# Revit family: W-Wide Flange-Column
name_source: partatom
category: Structural Columns
revit_build: Autodesk Revit Architecture 2012 (Build: 20110210_1515)
units: mm (PartAtom-declared; Revit-internal decimal feet)

## types (287) — shared parameters
Assembly Code = B10

## per-type parameters (varying)
| type | A | W | bf | d | k | kr | tf | tw |
| W44X335 | 98.5 in² | 335 | 1' - 3 7/8" | 3' - 8" | 0' - 2 5/8" | 0' - 0 7/8" | 0' - 1 3/4" | 0' - 1" |
| W44X290 | 85.4 in² | 290 | 1' - 3 13/16" | 3' - 7 5/8" | 0' - 2 7/16" | 0' - 0 7/8" | 0' - 1 9/16" | 0' - 0 7/8" |
| W44X262 | 76.9 in² | 262 | 1' - 3 13/16" | 3' - 7 5/16" | 0' - 2 1/4" | 0' - 0 13/16" | 0' - 1 7/16" | 0' - 0 13/16" |
| W44X230 | 67.7 in² | 230 | 1' - 3 13/16" | 3' - 6 7/8" | 0' - 2 1/16" | 0' - 0 13/16" | 0' - 1 1/4" | 0' - 0 11/16" |
| W40X593 | 174 in² | 593 | 1' - 4 11/16" | 3' - 7" | 0' - 4 1/2" | 0' - 1 1/4" | 0' - 3 1/4" | 0' - 1 13/16" |
| W40X503 | 148 in² | 503 | 1' - 4 3/8" | 3' - 6 1/8" | 0' - 4" | 0' - 1 1/4" | 0' - 2 3/4" | 0' - 1 9/16" |
| W40X431 | 127 in² | 431 | 1' - 4 3/16" | 3' - 5 5/16" | 0' - 3 5/8" | 0' - 1 1/4" | 0' - 2 3/8" | 0' - 1 5/16" |
| W40X397 | 117 in² | 397 | 1' - 4 1/8" | 3' - 5" | 0' - 3 1/2" | 0' - 1 5/16" | 0' - 2 3/16" | 0' - 1 1/4" |
| W40X372 | 109 in² | 372 | 1' - 4 1/8" | 3' - 4 5/8" | 0' - 3 5/16" | 0' - 1 1/4" | 0' - 2 1/16" | 0' - 1 3/16" |
| W40X362 | 107 in² | 362 | 1' - 4" | 3' - 4 5/8" | 0' - 3 1/4" | 0' - 1 1/4" | 0' - 2" | 0' - 1 1/8" |
| W40X324 | 95.3 in² | 324 | 1' - 3 7/8" | 3' - 4 3/16" | 0' - 3 1/16" | 0' - 1 1/4" | 0' - 1 13/16" | 0' - 1" |
| W40X297 | 87.4 in² | 297 | 1' - 3 13/16" | 3' - 3 13/16" | 0' - 2 15/16" | 0' - 1 5/16" | 0' - 1 5/8" | 0' - 0 15/16" |
| W40X277 | 81.4 in² | 277 | 1' - 3 13/16" | 3' - 3 11/16" | 0' - 2 7/8" | 0' - 1 5/16" | 0' - 1 9/16" | 0' - 0 13/16" |
| W40X249 | 73.3 in² | 249 | 1' - 3 13/16" | 3' - 3 3/8" | 0' - 2 11/16" | 0' - 1 1/4" | 0' - 1 7/16" | 0' - 0 3/4" |
| W40X215 | 63.4 in² | 215 | 1' - 3 13/16" | 3' - 3" | 0' - 2 1/2" | 0' - 1 1/4" | 0' - 1 1/4" | 0' - 0 5/8" |
| W40X199 | 58.5 in² | 199 | 1' - 3 13/16" | 3' - 2 11/16" | 0' - 2 5/16" | 0' - 1 1/4" | 0' - 1 1/16" | 0' - 0 5/8" |
| W40X392 | 115 in² | 392 | 1' - 0 3/8" | 3' - 5 5/8" | 0' - 3 13/16" | 0' - 1 5/16" | 0' - 2 1/2" | 0' - 1 7/16" |
| W40X331 | 97.5 in² | 331 | 1' - 0 3/16" | 3' - 4 13/16" | 0' - 3 3/8" | 0' - 1 1/4" | 0' - 2 1/8" | 0' - 1 1/4" |
| W40X327 | 96 in² | 327 | 1' - 0 1/8" | 3' - 4 13/16" | 0' - 3 3/8" | 0' - 1 1/4" | 0' - 2 1/8" | 0' - 1 3/16" |
| W40X294 | 86.3 in² | 294 | 1' - 0" | 3' - 4 3/8" | 0' - 3 3/16" | 0' - 1 1/4" | 0' - 1 15/16" | 0' - 1 1/16" |
| W40X278 | 82 in² | 278 | 1' - 0" | 3' - 4 3/16" | 0' - 3 1/16" | 0' - 1 1/4" | 0' - 1 13/16" | 0' - 1" |
| W40X264 | 77.6 in² | 264 | 0' - 11 7/8" | 3' - 4" | 0' - 3" | 0' - 1 1/4" | 0' - 1 3/4" | 0' - 0 15/16" |
| W40X235 | 69 in² | 235 | 0' - 11 7/8" | 3' - 3 11/16" | 0' - 2 7/8" | 0' - 1 5/16" | 0' - 1 9/16" | 0' - 0 13/16" |
| W40X211 | 62 in² | 211 | 0' - 11 13/16" | 3' - 3 3/8" | 0' - 2 11/16" | 0' - 1 1/4" | 0' - 1 7/16" | 0' - 0 3/4" |
| W40X183 | 53.3 in² | 183 | 0' - 11 13/16" | 3' - 3" | 0' - 2 1/2" | 0' - 1 5/16" | 0' - 1 3/16" | 0' - 0 5/8" |
| W40X167 | 49.2 in² | 167 | 0' - 11 13/16" | 3' - 2 5/8" | 0' - 2 5/16" | 0' - 1 5/16" | 0' - 1" | 0' - 0 5/8" |
| W40X149 | 43.8 in² | 149 | 0' - 11 13/16" | 3' - 2 3/16" | 0' - 2 1/8" | 0' - 1 5/16" | 0' - 0 13/16" | 0' - 0 5/8" |
| W36X798 - Obsolete | 235 in² | 798 | 1' - 6" | 3' - 6" | 0' - 5 9/16" | 0' - 1 1/4" | 0' - 4 5/16" | 0' - 2 3/8" |
| W36X650 - Obsolete | 191 in² | 650 | 1' - 5 9/16" | 3' - 4 1/2" | 0' - 4 13/16" | 0' - 1 1/4" | 0' - 3 9/16" | 0' - 2" |
| W36X527 - Obsolete | 155 in² | 527 | 1' - 5 1/4" | 3' - 3 3/16" | 0' - 4 3/16" | 0' - 1 1/4" | 0' - 2 15/16" | 0' - 1 5/8" |
| W36X439 - Obsolete | 129 in² | 439 | 1' - 4 15/16" | 3' - 2 1/4" | 0' - 3 11/16" | 0' - 1 1/4" | 0' - 2 7/16" | 0' - 1 3/8" |
| W36X393 - Obsolete | 116 in² | 393 | 1' - 4 13/16" | 3' - 1 13/16" | 0' - 3 7/16" | 0' - 1 1/4" | 0' - 2 3/16" | 0' - 1 1/4" |
| W36X359 - Obsolete | 105 in² | 359 | 1' - 4 3/4" | 3' - 1 3/8" | 0' - 3 1/4" | 0' - 1 1/4" | 0' - 2" | 0' - 1 1/8" |
| W36X328 - Obsolete | 96.4 in² | 328 | 1' - 4 5/8" | 3' - 1 1/16" | 0' - 3 1/8" | 0' - 1 1/4" | 0' - 1 7/8" | 0' - 1" |
| W36X300 - Obsolete | 88.3 in² | 300 | 1' - 4 5/8" | 3' - 0 3/4" | 0' - 2 15/16" | 0' - 1 1/4" | 0' - 1 11/16" | 0' - 0 15/16" |
| W36X280 - Obsolete | 82.4 in² | 280 | 1' - 4 5/8" | 3' - 0 1/2" | 0' - 2 13/16" | 0' - 1 1/4" | 0' - 1 9/16" | 0' - 0 7/8" |
| W36X260 - Obsolete | 76.5 in² | 260 | 1' - 4 9/16" | 3' - 0 1/4" | 0' - 2 11/16" | 0' - 1 1/4" | 0' - 1 7/16" | 0' - 0 13/16" |
| W36X245 - Obsolete | 72.1 in² | 245 | 1' - 4 1/2" | 3' - 0 1/16" | 0' - 2 5/8" | 0' - 1 1/4" | 0' - 1 3/8" | 0' - 0 13/16" |
| W36X230 - Obsolete | 67.6 in² | 230 | 1' - 4 1/2" | 2' - 11 7/8" | 0' - 2 1/2" | 0' - 1 1/4" | 0' - 1 1/4" | 0' - 0 3/4" |
| W36X800 | 236 in² | 800 | 1' - 6" | 3' - 6 5/8" | 0' - 5 9/16" | 0' - 1 1/4" | 0' - 4 5/16" | 0' - 2 3/8" |
| W36X652 | 192 in² | 652 | 1' - 5 5/8" | 3' - 5 1/8" | 0' - 4 13/16" | 0' - 1 1/4" | 0' - 3 9/16" | 0' - 2" |
| W36X529 | 156 in² | 529 | 1' - 5 3/16" | 3' - 3 13/16" | 0' - 4 3/16" | 0' - 1 1/4" | 0' - 2 15/16" | 0' - 1 5/8" |
| W36X487 | 143 in² | 487 | 1' - 5 1/8" | 3' - 3 5/16" | 0' - 4" | 0' - 1 5/16" | 0' - 2 11/16" | 0' - 1 1/2" |
| W36X441 | 130 in² | 442 | 1' - 5" | 3' - 2 7/8" | 0' - 3 3/4" | 0' - 1 5/16" | 0' - 2 7/16" | 0' - 1 3/8" |
| W36X395 | 116 in² | 395 | 1' - 4 13/16" | 3' - 2 3/8" | 0' - 3 7/16" | 0' - 1 1/4" | 0' - 2 3/16" | 0' - 1 1/4" |
| W36X361 | 106 in² | 361 | 1' - 4 11/16" | 3' - 2" | 0' - 3 5/16" | 0' - 1 5/16" | 0' - 2" | 0' - 1 1/8" |
| W36X330 | 97 in² | 330 | 1' - 4 5/8" | 3' - 1 11/16" | 0' - 3 1/8" | 0' - 1 1/4" | 0' - 1 7/8" | 0' - 1" |
| W36X302 | 88.8 in² | 302 | 1' - 4 11/16" | 3' - 1 5/16" | 0' - 3" | 0' - 1 5/16" | 0' - 1 11/16" | 0' - 0 15/16" |
| W36X282 | 82.9 in² | 282 | 1' - 4 5/8" | 3' - 1 1/8" | 0' - 2 7/8" | 0' - 1 5/16" | 0' - 1 9/16" | 0' - 0 7/8" |
| W36X262 | 77 in² | 262 | 1' - 4 5/8" | 3' - 0 7/8" | 0' - 2 3/4" | 0' - 1 5/16" | 0' - 1 7/16" | 0' - 0 13/16" |
| W36X247 | 72.5 in² | 247 | 1' - 4 1/2" | 3' - 0 11/16" | 0' - 2 5/8" | 0' - 1 1/4" | 0' - 1 3/8" | 0' - 0 13/16" |
| W36X231 | 68.1 in² | 230 | 1' - 4 1/2" | 3' - 0 1/2" | 0' - 2 9/16" | 0' - 1 5/16" | 0' - 1 1/4" | 0' - 0 3/4" |
| W36X256 | 75.4 in² | 256 | 1' - 0 3/16" | 3' - 1 3/8" | 0' - 2 5/8" | 0' - 0 7/8" | 0' - 1 3/4" | 0' - 0 15/16" |
| W36X232 | 68.1 in² | 232 | 1' - 0 1/8" | 3' - 1 1/8" | 0' - 2 7/16" | 0' - 0 7/8" | 0' - 1 9/16" | 0' - 0 7/8" |
| W36X210 | 61.8 in² | 210 | 1' - 0 3/16" | 3' - 0 11/16" | 0' - 2 5/16" | 0' - 0 15/16" | 0' - 1 3/8" | 0' - 0 13/16" |
| W36X194 | 57 in² | 194 | 1' - 0 1/8" | 3' - 0 1/2" | 0' - 2 3/16" | 0' - 0 15/16" | 0' - 1 1/4" | 0' - 0 3/4" |
| W36X182 | 53.6 in² | 182 | 1' - 0 1/8" | 3' - 0 5/16" | 0' - 2 1/8" | 0' - 0 15/16" | 0' - 1 3/16" | 0' - 0 3/4" |
| W36X170 | 50.1 in² | 170 | 1' - 0" | 3' - 0 3/16" | 0' - 2" | 0' - 0 7/8" | 0' - 1 1/8" | 0' - 0 11/16" |
| W36X160 | 47 in² | 160 | 1' - 0" | 3' - 0" | 0' - 1 15/16" | 0' - 0 15/16" | 0' - 1" | 0' - 0 5/8" |
| W36X150 | 44.2 in² | 150 | 1' - 0" | 2' - 11 7/8" | 0' - 1 7/8" | 0' - 0 15/16" | 0' - 0 15/16" | 0' - 0 5/8" |
| W36X135 | 39.7 in² | 135 | 1' - 0" | 2' - 11 5/8" | 0' - 1 11/16" | 0' - 0 7/8" | 0' - 0 13/16" | 0' - 0 5/8" |
| W33X387 | 114 in² | 387 | 1' - 4 3/16" | 3' - 0" | 0' - 3 3/16" | 0' - 0 15/16" | 0' - 2 1/4" | 0' - 1 1/4" |
| W33X354 | 104 in² | 354 | 1' - 4 1/8" | 2' - 11 5/8" | 0' - 2 15/16" | 0' - 0 7/8" | 0' - 2 1/16" | 0' - 1 3/16" |
| W33X318 | 93.6 in² | 318 | 1' - 4" | 2' - 11 3/16" | 0' - 2 3/4" | 0' - 0 7/8" | 0' - 1 7/8" | 0' - 1 1/16" |
| W33X291 | 85.7 in² | 291 | 1' - 3 7/8" | 2' - 10 13/16" | 0' - 2 5/8" | 0' - 0 7/8" | 0' - 1 3/4" | 0' - 0 15/16" |
| W33X263 | 77.5 in² | 263 | 1' - 3 13/16" | 2' - 10 1/2" | 0' - 2 7/16" | 0' - 0 7/8" | 0' - 1 9/16" | 0' - 0 7/8" |
| W33X241 | 71 in² | 241 | 1' - 3 7/8" | 2' - 10 3/16" | 0' - 2 1/4" | 0' - 0 7/8" | 0' - 1 3/8" | 0' - 0 13/16" |
| W33X221 | 65.2 in² | 221 | 1' - 3 13/16" | 2' - 9 7/8" | 0' - 2 1/8" | 0' - 0 7/8" | 0' - 1 1/4" | 0' - 0 3/4" |
| W33X201 | 59.2 in² | 201 | 1' - 3 11/16" | 2' - 9 11/16" | 0' - 2" | 0' - 0 7/8" | 0' - 1 1/8" | 0' - 0 11/16" |
| W33X169 | 49.5 in² | 169 | 0' - 11 1/2" | 2' - 9 13/16" | 0' - 2 1/8" | 0' - 0 7/8" | 0' - 1 1/4" | 0' - 0 11/16" |
| W33X152 | 44.8 in² | 152 | 0' - 11 5/8" | 2' - 9 1/2" | 0' - 1 15/16" | 0' - 0 7/8" | 0' - 1 1/16" | 0' - 0 5/8" |
| W33X141 | 41.6 in² | 141 | 0' - 11 1/2" | 2' - 9 5/16" | 0' - 1 13/16" | 0' - 0 7/8" | 0' - 0 15/16" | 0' - 0 5/8" |
| W33X130 | 38.3 in² | 130 | 0' - 11 1/2" | 2' - 9 1/8" | 0' - 1 3/4" | 0' - 0 7/8" | 0' - 0 7/8" | 0' - 0 9/16" |
| W33X118 | 34.7 in² | 118 | 0' - 11 1/2" | 2' - 8 7/8" | 0' - 1 5/8" | 0' - 0 7/8" | 0' - 0 3/4" | 0' - 0 9/16" |
| W30X391 | 115 in² | 391 | 1' - 3 5/8" | 2' - 9 3/16" | 0' - 3 3/8" | 0' - 0 15/16" | 0' - 2 7/16" | 0' - 1 3/8" |
| W30X357 | 105 in² | 357 | 1' - 3 1/2" | 2' - 8 13/16" | 0' - 3 1/8" | 0' - 0 7/8" | 0' - 2 1/4" | 0' - 1 1/4" |
| W30X326 | 95.8 in² | 326 | 1' - 3 3/8" | 2' - 8 3/8" | 0' - 2 15/16" | 0' - 0 7/8" | 0' - 2 1/16" | 0' - 1 1/8" |
| W30X292 | 85.9 in² | 292 | 1' - 3 5/16" | 2' - 8" | 0' - 2 3/4" | 0' - 0 7/8" | 0' - 1 7/8" | 0' - 1" |
| W30X261 | 76.9 in² | 261 | 1' - 3 3/16" | 2' - 7 5/8" | 0' - 2 9/16" | 0' - 0 15/16" | 0' - 1 5/8" | 0' - 0 15/16" |
| W30X235 | 69.2 in² | 235 | 1' - 3 1/8" | 2' - 7 5/16" | 0' - 2 3/8" | 0' - 0 7/8" | 0' - 1 1/2" | 0' - 0 13/16" |
| W30X211 | 62.2 in² | 211 | 1' - 3 1/8" | 2' - 6 7/8" | 0' - 2 1/4" | 0' - 0 15/16" | 0' - 1 5/16" | 0' - 0 3/4" |
| W30X191 | 56.3 in² | 191 | 1' - 3" | 2' - 6 11/16" | 0' - 2 1/16" | 0' - 0 7/8" | 0' - 1 3/16" | 0' - 0 11/16" |
| W30X173 | 51 in² | 173 | 1' - 3" | 2' - 6 3/8" | 0' - 2" | 0' - 0 15/16" | 0' - 1 1/16" | 0' - 0 5/8" |
| W30X148 | 43.5 in² | 148 | 0' - 10 1/2" | 2' - 6 11/16" | 0' - 2 1/16" | 0' - 0 7/8" | 0' - 1 3/16" | 0' - 0 5/8" |
| W30X132 | 38.9 in² | 132 | 0' - 10 1/2" | 2' - 6 5/16" | 0' - 1 7/8" | 0' - 0 7/8" | 0' - 1" | 0' - 0 5/8" |
| W30X124 | 36.5 in² | 124 | 0' - 10 1/2" | 2' - 6 3/16" | 0' - 1 13/16" | 0' - 0 7/8" | 0' - 0 15/16" | 0' - 0 9/16" |
| W30X116 | 34.2 in² | 116 | 0' - 10 1/2" | 2' - 6" | 0' - 1 3/4" | 0' - 0 7/8" | 0' - 0 7/8" | 0' - 0 9/16" |
| W30X108 | 31.7 in² | 108 | 0' - 10 1/2" | 2' - 5 13/16" | 0' - 1 11/16" | 0' - 0 15/16" | 0' - 0 3/4" | 0' - 0 9/16" |
| W30X99 | 29.1 in² | 99 | 0' - 10 1/2" | 2' - 5 11/16" | 0' - 1 9/16" | 0' - 0 7/8" | 0' - 0 11/16" | 0' - 0 1/2" |
| W30X90 | 26.4 in² | 90 | 0' - 10 3/8" | 2' - 5 1/2" | 0' - 1 1/2" | 0' - 0 7/8" | 0' - 0 5/8" | 0' - 0 1/2" |
| W27X539 | 159 in² | 539 | 1' - 3 5/16" | 2' - 8 1/2" | 0' - 4 7/16" | 0' - 0 7/8" | 0' - 3 9/16" | 0' - 2" |
| W27X368 | 108 in² | 368 | 1' - 2 11/16" | 2' - 6 3/8" | 0' - 3 3/8" | 0' - 0 7/8" | 0' - 2 1/2" | 0' - 1 3/8" |
| W27X336 | 98.9 in² | 336 | 1' - 2 5/8" | 2' - 6" | 0' - 3 3/16" | 0' - 0 15/16" | 0' - 2 1/4" | 0' - 1 1/4" |
| W27X307 | 90.4 in² | 307 | 1' - 2 3/8" | 2' - 5 5/8" | 0' - 3" | 0' - 0 15/16" | 0' - 2 1/16" | 0' - 1 3/16" |
| W27X281 | 82.9 in² | 281 | 1' - 2 3/8" | 2' - 5 5/16" | 0' - 2 13/16" | 0' - 0 7/8" | 0' - 1 15/16" | 0' - 1 1/16" |
| W27X258 | 76 in² | 258 | 1' - 2 5/16" | 2' - 5" | 0' - 2 11/16" | 0' - 0 15/16" | 0' - 1 3/4" | 0' - 1" |
| W27X235 | 69.4 in² | 235 | 1' - 2 3/16" | 2' - 4 11/16" | 0' - 2 1/2" | 0' - 0 7/8" | 0' - 1 5/8" | 0' - 0 15/16" |
| W27X217 | 64 in² | 217 | 1' - 2 1/8" | 2' - 4 3/8" | 0' - 2 3/8" | 0' - 0 7/8" | 0' - 1 1/2" | 0' - 0 13/16" |
| W27X194 | 57.2 in² | 194 | 1' - 2" | 2' - 4 1/8" | 0' - 2 1/4" | 0' - 0 15/16" | 0' - 1 5/16" | 0' - 0 3/4" |
| W27X178 | 52.5 in² | 178 | 1' - 2 1/8" | 2' - 3 13/16" | 0' - 2 1/16" | 0' - 0 7/8" | 0' - 1 3/16" | 0' - 0 3/4" |
| W27X161 | 47.6 in² | 161 | 1' - 2" | 2' - 3 5/8" | 0' - 2" | 0' - 0 15/16" | 0' - 1 1/16" | 0' - 0 11/16" |
| W27X146 | 43.1 in² | 146 | 1' - 2" | 2' - 3 3/8" | 0' - 1 7/8" | 0' - 0 7/8" | 0' - 1" | 0' - 0 5/8" |
| W27X129 | 37.8 in² | 129 | 0' - 10" | 2' - 3 5/8" | 0' - 2" | 0' - 0 7/8" | 0' - 1 1/8" | 0' - 0 5/8" |
| W27X114 | 33.5 in² | 114 | 0' - 10 1/8" | 2' - 3 5/16" | 0' - 1 13/16" | 0' - 0 7/8" | 0' - 0 15/16" | 0' - 0 9/16" |
| W27X102 | 30 in² | 102 | 0' - 10" | 2' - 3 1/8" | 0' - 1 3/4" | 0' - 0 15/16" | 0' - 0 13/16" | 0' - 0 1/2" |
| W27X94 | 27.7 in² | 94 | 0' - 10" | 2' - 2 7/8" | 0' - 1 5/8" | 0' - 0 7/8" | 0' - 0 3/4" | 0' - 0 1/2" |
| W27X84 | 24.8 in² | 84 | 0' - 10" | 2' - 2 11/16" | 0' - 1 9/16" | 0' - 0 15/16" | 0' - 0 5/8" | 0' - 0 7/16" |
| W24X370 | 109 in² | 370 | 1' - 1 11/16" | 2' - 4" | 0' - 3 5/8" | 0' - 0 7/8" | 0' - 2 3/4" | 0' - 1 1/2" |
| W24X335 | 98.4 in² | 335 | 1' - 1 1/2" | 2' - 3 1/2" | 0' - 3 3/8" | 0' - 0 7/8" | 0' - 2 1/2" | 0' - 1 3/8" |
| W24X306 | 89.8 in² | 306 | 1' - 1 3/8" | 2' - 3 1/8" | 0' - 3 3/16" | 0' - 0 15/16" | 0' - 2 1/4" | 0' - 1 1/4" |
| W24X279 | 82 in² | 279 | 1' - 1 5/16" | 2' - 2 11/16" | 0' - 3" | 0' - 0 15/16" | 0' - 2 1/16" | 0' - 1 3/16" |
| W24X250 | 73.5 in² | 250 | 1' - 1 3/16" | 2' - 2 5/16" | 0' - 2 13/16" | 0' - 0 15/16" | 0' - 1 7/8" | 0' - 1 1/16" |
| W24X229 | 67.2 in² | 229 | 1' - 1 1/8" | 2' - 2" | 0' - 2 5/8" | 0' - 0 7/8" | 0' - 1 3/4" | 0' - 0 15/16" |
| W24X207 | 60.7 in² | 207 | 1' - 1" | 2' - 1 11/16" | 0' - 2 1/2" | 0' - 0 15/16" | 0' - 1 9/16" | 0' - 0 7/8" |
| W24X192 | 56.3 in² | 192 | 1' - 1" | 2' - 1 1/2" | 0' - 2 3/8" | 0' - 0 15/16" | 0' - 1 7/16" | 0' - 0 13/16" |
| W24X176 | 51.7 in² | 176 | 1' - 0 7/8" | 2' - 1 3/16" | 0' - 2 1/4" | 0' - 0 15/16" | 0' - 1 5/16" | 0' - 0 3/4" |
| W24X162 | 47.7 in² | 162 | 1' - 1" | 2' - 1" | 0' - 2 1/8" | 0' - 0 7/8" | 0' - 1 1/4" | 0' - 0 11/16" |
| W24X146 | 43 in² | 146 | 1' - 0 7/8" | 2' - 0 11/16" | 0' - 2" | 0' - 0 15/16" | 0' - 1 1/16" | 0' - 0 5/8" |
| W24X131 | 38.5 in² | 131 | 1' - 0 7/8" | 2' - 0 1/2" | 0' - 1 7/8" | 0' - 0 15/16" | 0' - 0 15/16" | 0' - 0 5/8" |
| W24X117 | 34.4 in² | 117 | 1' - 0 13/16" | 2' - 0 5/16" | 0' - 1 3/4" | 0' - 0 7/8" | 0' - 0 7/8" | 0' - 0 9/16" |
| W24X104 | 30.6 in² | 104 | 1' - 0 13/16" | 2' - 0 1/8" | 0' - 1 5/8" | 0' - 0 7/8" | 0' - 0 3/4" | 0' - 0 1/2" |
| W24X103 | 30.3 in² | 103 | 0' - 9" | 2' - 0 1/2" | 0' - 1 7/8" | 0' - 0 7/8" | 0' - 1" | 0' - 0 9/16" |
| W24X94 | 27.7 in² | 94 | 0' - 9 1/16" | 2' - 0 5/16" | 0' - 1 3/4" | 0' - 0 7/8" | 0' - 0 7/8" | 0' - 0 1/2" |
| W24X84 | 24.7 in² | 84 | 0' - 9" | 2' - 0 1/8" | 0' - 1 11/16" | 0' - 0 15/16" | 0' - 0 3/4" | 0' - 0 1/2" |
| W24X76 | 22.4 in² | 76 | 0' - 9" | 1' - 11 7/8" | 0' - 1 9/16" | 0' - 0 7/8" | 0' - 0 11/16" | 0' - 0 7/16" |
| W24X68 | 20.1 in² | 68 | 0' - 9" | 1' - 11 11/16" | 0' - 1 1/2" | 0' - 0 15/16" | 0' - 0 9/16" | 0' - 0 7/16" |
| W24X62 | 18.2 in² | 62 | 0' - 7 1/16" | 1' - 11 11/16" | 0' - 1 1/2" | 0' - 0 15/16" | 0' - 0 9/16" | 0' - 0 7/16" |
| W24X55 | 16.2 in² | 55 | 0' - 7" | 1' - 11 5/8" | 0' - 1 7/16" | 0' - 0 15/16" | 0' - 0 1/2" | 0' - 0 3/8" |
| W21X201 | 59.2 in² | 201 | 1' - 0 5/8" | 1' - 11" | 0' - 2 1/2" | 0' - 0 7/8" | 0' - 1 5/8" | 0' - 0 15/16" |
| W21X182 | 53.6 in² | 182 | 1' - 0 1/2" | 1' - 10 11/16" | 0' - 2 3/8" | 0' - 0 7/8" | 0' - 1 1/2" | 0' - 0 13/16" |
| W21X166 | 48.8 in² | 166 | 1' - 0 3/8" | 1' - 10 1/2" | 0' - 2 1/4" | 0' - 0 7/8" | 0' - 1 3/8" | 0' - 0 3/4" |
| W21X147 | 43.2 in² | 147 | 1' - 0 1/2" | 1' - 10 1/8" | 0' - 2" | 0' - 0 7/8" | 0' - 1 1/8" | 0' - 0 3/4" |
| W21X132 | 38.8 in² | 132 | 1' - 0 3/8" | 1' - 9 13/16" | 0' - 1 15/16" | 0' - 0 7/8" | 0' - 1 1/16" | 0' - 0 5/8" |
| W21X122 | 35.9 in² | 122 | 1' - 0 3/8" | 1' - 9 11/16" | 0' - 1 13/16" | 0' - 0 7/8" | 0' - 0 15/16" | 0' - 0 5/8" |
| W21X111 | 32.7 in² | 111 | 1' - 0 5/16" | 1' - 9 1/2" | 0' - 1 3/4" | 0' - 0 7/8" | 0' - 0 7/8" | 0' - 0 9/16" |
| W21X101 | 29.8 in² | 101 | 1' - 0 5/16" | 1' - 9 3/8" | 0' - 1 11/16" | 0' - 0 7/8" | 0' - 0 13/16" | 0' - 0 1/2" |
| W21X93 | 27.3 in² | 93 | 0' - 8 7/16" | 1' - 9 5/8" | 0' - 1 5/8" | 0' - 0 11/16" | 0' - 0 15/16" | 0' - 0 9/16" |
| W21X83 | 24.3 in² | 83 | 0' - 8 3/8" | 1' - 9 3/8" | 0' - 1 1/2" | 0' - 0 11/16" | 0' - 0 13/16" | 0' - 0 1/2" |
| W21X73 | 21.5 in² | 73 | 0' - 8 5/16" | 1' - 9 3/16" | 0' - 1 7/16" | 0' - 0 11/16" | 0' - 0 3/4" | 0' - 0 7/16" |
| W21X68 | 20 in² | 68 | 0' - 8 1/4" | 1' - 9 1/8" | 0' - 1 3/8" | 0' - 0 11/16" | 0' - 0 11/16" | 0' - 0 7/16" |
| W21X62 | 18.3 in² | 62 | 0' - 8 1/4" | 1' - 9" | 0' - 1 5/16" | 0' - 0 11/16" | 0' - 0 5/8" | 0' - 0 3/8" |
| W21X55 | 16.2 in² | 55 | 0' - 8 1/4" | 1' - 8 13/16" | 0' - 1 3/16" | 0' - 0 11/16" | 0' - 0 1/2" | 0' - 0 3/8" |
| W21X48 | 14.1 in² | 48 | 0' - 8 1/8" | 1' - 8 5/8" | 0' - 1 1/8" | 0' - 0 11/16" | 0' - 0 7/16" | 0' - 0 3/8" |
| W21X57 | 16.7 in² | 57 | 0' - 6 9/16" | 1' - 9 1/8" | 0' - 1 5/16" | 0' - 0 11/16" | 0' - 0 5/8" | 0' - 0 3/8" |
| W21X50 | 14.7 in² | 50 | 0' - 6 1/2" | 1' - 8 13/16" | 0' - 1 1/4" | 0' - 0 11/16" | 0' - 0 9/16" | 0' - 0 3/8" |
| W21X44 | 13 in² | 44 | 0' - 6 1/2" | 1' - 8 11/16" | 0' - 1 1/8" | 0' - 0 11/16" | 0' - 0 7/16" | 0' - 0 3/8" |
| W18x311 | 91.6 in² | 311 | 1' - 0" | 1' - 10 5/16" | 0' - 3 7/16" | 0' - 0 11/16" | 0' - 2 3/4" | 0' - 1 1/2" |
| W18x283 | 83.3 in² | 283 | 0' - 11 7/8" | 1' - 9 7/8" | 0' - 3 3/16" | 0' - 0 11/16" | 0' - 2 1/2" | 0' - 1 3/8" |
| W18x258 | 75.9 in² | 258 | 0' - 11 13/16" | 1' - 9 1/2" | 0' - 3" | 0' - 0 11/16" | 0' - 2 5/16" | 0' - 1 1/4" |
| W18x234 | 68.8 in² | 234 | 0' - 11 11/16" | 1' - 9 1/8" | 0' - 2 3/4" | 0' - 0 5/8" | 0' - 2 1/8" | 0' - 1 3/16" |
| W18x211 | 62.1 in² | 211 | 0' - 11 5/8" | 1' - 8 11/16" | 0' - 2 9/16" | 0' - 0 5/8" | 0' - 1 15/16" | 0' - 1 1/16" |
| W18x192 | 56.4 in² | 192 | 0' - 11 1/2" | 1' - 8 3/8" | 0' - 2 7/16" | 0' - 0 11/16" | 0' - 1 3/4" | 0' - 0 15/16" |
| W18X175 | 51.3 in² | 175 | 0' - 11 3/8" | 1' - 8" | 0' - 2 7/16" | 0' - 0 7/8" | 0' - 1 9/16" | 0' - 0 7/8" |
| W18X158 | 46.3 in² | 158 | 0' - 11 5/16" | 1' - 7 11/16" | 0' - 2 3/8" | 0' - 0 15/16" | 0' - 1 7/16" | 0' - 0 13/16" |
| W18X143 | 42.1 in² | 143 | 0' - 11 3/16" | 1' - 7 1/2" | 0' - 2 3/16" | 0' - 0 7/8" | 0' - 1 5/16" | 0' - 0 3/4" |
| W18X130 | 38.2 in² | 130 | 0' - 11 3/16" | 1' - 7 5/16" | 0' - 2 1/16" | 0' - 0 7/8" | 0' - 1 3/16" | 0' - 0 11/16" |
| W18X119 | 35.1 in² | 119 | 0' - 11 5/16" | 1' - 7" | 0' - 1 15/16" | 0' - 0 7/8" | 0' - 1 1/16" | 0' - 0 5/8" |
| W18X106 | 31.1 in² | 106 | 0' - 11 3/16" | 1' - 6 11/16" | 0' - 1 13/16" | 0' - 0 7/8" | 0' - 0 15/16" | 0' - 0 9/16" |
| W18X97 | 28.5 in² | 97 | 0' - 11 1/8" | 1' - 6 5/8" | 0' - 1 3/4" | 0' - 0 7/8" | 0' - 0 7/8" | 0' - 0 9/16" |
| W18X86 | 25.3 in² | 86 | 0' - 11 1/8" | 1' - 6 3/8" | 0' - 1 5/8" | 0' - 0 7/8" | 0' - 0 3/4" | 0' - 0 1/2" |
| W18X76 | 22.3 in² | 76 | 0' - 11" | 1' - 6 3/16" | 0' - 1 9/16" | 0' - 0 7/8" | 0' - 0 11/16" | 0' - 0 7/16" |
| W18X71 | 20.8 in² | 71 | 0' - 7 5/8" | 1' - 6 1/2" | 0' - 1 1/2" | 0' - 0 11/16" | 0' - 0 13/16" | 0' - 0 1/2" |
| W18X65 | 19.1 in² | 65 | 0' - 7 9/16" | 1' - 6 3/8" | 0' - 1 7/16" | 0' - 0 11/16" | 0' - 0 3/4" | 0' - 0 7/16" |
| W18X60 | 17.6 in² | 60 | 0' - 7 9/16" | 1' - 6 3/16" | 0' - 1 3/8" | 0' - 0 11/16" | 0' - 0 11/16" | 0' - 0 7/16" |
| W18X55 | 16.2 in² | 55 | 0' - 7 1/2" | 1' - 6 1/8" | 0' - 1 5/16" | 0' - 0 11/16" | 0' - 0 5/8" | 0' - 0 3/8" |
| W18X50 | 14.7 in² | 50 | 0' - 7 1/2" | 1' - 6" | 0' - 1 1/4" | 0' - 0 11/16" | 0' - 0 9/16" | 0' - 0 3/8" |
| W18X46 | 13.5 in² | 46 | 0' - 6 1/16" | 1' - 6 1/8" | 0' - 1 1/4" | 0' - 0 5/8" | 0' - 0 5/8" | 0' - 0 3/8" |
| W18X40 | 11.8 in² | 40 | 0' - 6" | 1' - 5 7/8" | 0' - 1 3/16" | 0' - 0 11/16" | 0' - 0 1/2" | 0' - 0 5/16" |
| W18X35 | 10.3 in² | 35 | 0' - 6" | 1' - 5 11/16" | 0' - 1 1/8" | 0' - 0 11/16" | 0' - 0 7/16" | 0' - 0 5/16" |
| W16X100 | 29.5 in² | 100 | 0' - 10 3/8" | 1' - 5" | 0' - 1 7/8" | 0' - 0 7/8" | 0' - 1" | 0' - 0 9/16" |
| W16X89 | 26.2 in² | 89 | 0' - 10 3/8" | 1' - 4 13/16" | 0' - 1 3/4" | 0' - 0 7/8" | 0' - 0 7/8" | 0' - 0 1/2" |
| W16X77 | 22.6 in² | 77 | 0' - 10 5/16" | 1' - 4 1/2" | 0' - 1 5/8" | 0' - 0 7/8" | 0' - 0 3/4" | 0' - 0 7/16" |
| W16X67 | 19.7 in² | 67 | 0' - 10 3/16" | 1' - 4 5/16" | 0' - 1 9/16" | 0' - 0 7/8" | 0' - 0 11/16" | 0' - 0 3/8" |
| W16X57 | 16.8 in² | 57 | 0' - 7 1/8" | 1' - 4 3/8" | 0' - 1 3/8" | 0' - 0 11/16" | 0' - 0 11/16" | 0' - 0 7/16" |
| W16X50 | 14.7 in² | 50 | 0' - 7 1/16" | 1' - 4 5/16" | 0' - 1 5/16" | 0' - 0 11/16" | 0' - 0 5/8" | 0' - 0 3/8" |
| W16X45 | 13.3 in² | 45 | 0' - 7 1/16" | 1' - 4 1/8" | 0' - 1 1/4" | 0' - 0 11/16" | 0' - 0 9/16" | 0' - 0 3/8" |
| W16X40 | 11.8 in² | 40 | 0' - 7" | 1' - 4" | 0' - 1 3/16" | 0' - 0 11/16" | 0' - 0 1/2" | 0' - 0 5/16" |
| W16X36 | 10.6 in² | 36 | 0' - 7" | 1' - 3 7/8" | 0' - 1 1/8" | 0' - 0 11/16" | 0' - 0 7/16" | 0' - 0 5/16" |
| W16X31 | 9.13 in² | 31 | 0' - 5 1/2" | 1' - 3 7/8" | 0' - 1 1/8" | 0' - 0 11/16" | 0' - 0 7/16" | 0' - 0 1/4" |
| W16X26 | 7.68 in² | 26 | 0' - 5 1/2" | 1' - 3 11/16" | 0' - 1 1/16" | 0' - 0 11/16" | 0' - 0 3/8" | 0' - 0 1/4" |
| W14X808 - Obsolete | 237 in² | 808 | 1' - 6 9/16" | 1' - 10 13/16" | 0' - 6 7/16" | 0' - 1 5/16" | 0' - 5 1/8" | 0' - 3 3/4" |
| W14X730 | 215 in² | 730 | 1' - 5 7/8" | 1' - 10 3/8" | 0' - 6 3/16" | 0' - 1 1/4" | 0' - 4 15/16" | 0' - 3 1/16" |
| W14X665 | 196 in² | 665 | 1' - 5 11/16" | 1' - 9 5/8" | 0' - 5 13/16" | 0' - 1 5/16" | 0' - 4 1/2" | 0' - 2 13/16" |
| W14X605 | 178 in² | 605 | 1' - 5 3/8" | 1' - 8 7/8" | 0' - 5 7/16" | 0' - 1 1/4" | 0' - 4 3/16" | 0' - 2 5/8" |
| W14X550 | 162 in² | 550 | 1' - 5 3/16" | 1' - 8 3/16" | 0' - 5 1/8" | 0' - 1 5/16" | 0' - 3 13/16" | 0' - 2 3/8" |
| W14X500 | 147 in² | 500 | 1' - 5" | 1' - 7 5/8" | 0' - 4 13/16" | 0' - 1 5/16" | 0' - 3 1/2" | 0' - 2 3/16" |
| W14X455 | 134 in² | 455 | 1' - 4 13/16" | 1' - 7" | 0' - 4 1/2" | 0' - 1 5/16" | 0' - 3 3/16" | 0' - 2" |
| W14X426 | 125 in² | 426 | 1' - 4 11/16" | 1' - 6 11/16" | 0' - 4 5/16" | 0' - 1 1/4" | 0' - 3 1/16" | 0' - 1 7/8" |
| W14X398 | 117 in² | 398 | 1' - 4 5/8" | 1' - 6 5/16" | 0' - 4 1/8" | 0' - 1 1/4" | 0' - 2 7/8" | 0' - 1 3/4" |
| W14X370 | 109 in² | 370 | 1' - 4 1/2" | 1' - 5 7/8" | 0' - 3 15/16" | 0' - 1 1/4" | 0' - 2 11/16" | 0' - 1 11/16" |
| W14X342 | 101 in² | 342 | 1' - 4 3/8" | 1' - 5 1/2" | 0' - 3 3/4" | 0' - 1 1/4" | 0' - 2 1/2" | 0' - 1 9/16" |
| W14X311 | 91.4 in² | 311 | 1' - 4 3/16" | 1' - 5 1/8" | 0' - 3 9/16" | 0' - 1 5/16" | 0' - 2 1/4" | 0' - 1 7/16" |
| W14X283 | 83.3 in² | 283 | 1' - 4 1/8" | 1' - 4 11/16" | 0' - 3 3/8" | 0' - 1 5/16" | 0' - 2 1/16" | 0' - 1 5/16" |
| W14X257 | 75.6 in² | 257 | 1' - 4" | 1' - 4 3/8" | 0' - 3 3/16" | 0' - 1 5/16" | 0' - 1 7/8" | 0' - 1 3/16" |
| W14X233 | 68.5 in² | 233 | 1' - 3 7/8" | 1' - 4" | 0' - 3" | 0' - 1 1/4" | 0' - 1 3/4" | 0' - 1 1/16" |
| W14X211 | 62 in² | 211 | 1' - 3 13/16" | 1' - 3 11/16" | 0' - 2 7/8" | 0' - 1 5/16" | 0' - 1 9/16" | 0' - 1" |
| W14X193 | 56.8 in² | 193 | 1' - 3 11/16" | 1' - 3 1/2" | 0' - 2 3/4" | 0' - 1 5/16" | 0' - 1 7/16" | 0' - 0 7/8" |
| W14X176 | 51.8 in² | 176 | 1' - 3 11/16" | 1' - 3 3/16" | 0' - 2 5/8" | 0' - 1 5/16" | 0' - 1 5/16" | 0' - 0 13/16" |
| W14X159 | 46.7 in² | 159 | 1' - 3 5/8" | 1' - 3" | 0' - 2 1/2" | 0' - 1 5/16" | 0' - 1 3/16" | 0' - 0 3/4" |
| W14X145 | 42.7 in² | 145 | 1' - 3 1/2" | 1' - 2 13/16" | 0' - 2 3/8" | 0' - 1 5/16" | 0' - 1 1/16" | 0' - 0 11/16" |
| W14X132 | 38.8 in² | 132 | 1' - 2 11/16" | 1' - 2 11/16" | 0' - 2 5/16" | 0' - 1 5/16" | 0' - 1" | 0' - 0 5/8" |
| W14X120 | 35.3 in² | 120 | 1' - 2 11/16" | 1' - 2 1/2" | 0' - 2 1/4" | 0' - 1 5/16" | 0' - 0 15/16" | 0' - 0 9/16" |
| W14X109 | 32 in² | 109 | 1' - 2 5/8" | 1' - 2 5/16" | 0' - 2 3/16" | 0' - 1 5/16" | 0' - 0 7/8" | 0' - 0 1/2" |
| W14X99 | 29.1 in² | 99 | 1' - 2 5/8" | 1' - 2 3/16" | 0' - 2 1/16" | 0' - 1 5/16" | 0' - 0 3/4" | 0' - 0 1/2" |
| W14X90 | 26.5 in² | 90 | 1' - 2 1/2" | 1' - 2" | 0' - 2" | 0' - 1 5/16" | 0' - 0 11/16" | 0' - 0 7/16" |
| W14X82 | 24 in² | 82 | 0' - 10 1/8" | 1' - 2 5/16" | 0' - 1 11/16" | 0' - 0 13/16" | 0' - 0 7/8" | 0' - 0 1/2" |
| W14X74 | 21.8 in² | 74 | 0' - 10 1/8" | 1' - 2 3/16" | 0' - 1 5/8" | 0' - 0 13/16" | 0' - 0 13/16" | 0' - 0 7/16" |
| W14X68 | 20 in² | 68 | 0' - 10" | 1' - 2" | 0' - 1 9/16" | 0' - 0 13/16" | 0' - 0 3/4" | 0' - 0 7/16" |
| W14X61 | 17.9 in² | 61 | 0' - 10" | 1' - 1 7/8" | 0' - 1 1/2" | 0' - 0 7/8" | 0' - 0 5/8" | 0' - 0 3/8" |
| W14X53 | 15.6 in² | 53 | 0' - 8 1/16" | 1' - 1 7/8" | 0' - 1 1/2" | 0' - 0 13/16" | 0' - 0 11/16" | 0' - 0 3/8" |
| W14X48 | 14.1 in² | 48 | 0' - 8" | 1' - 1 13/16" | 0' - 1 7/16" | 0' - 0 13/16" | 0' - 0 5/8" | 0' - 0 5/16" |
| W14X43 | 12.6 in² | 43 | 0' - 8" | 1' - 1 11/16" | 0' - 1 3/8" | 0' - 0 7/8" | 0' - 0 1/2" | 0' - 0 5/16" |
| W14X38 | 11.2 in² | 38 | 0' - 6 3/4" | 1' - 2 1/8" | 0' - 1 1/4" | 0' - 0 3/4" | 0' - 0 1/2" | 0' - 0 5/16" |
| W14X34 | 10 in² | 34 | 0' - 6 3/4" | 1' - 2" | 0' - 1 3/16" | 0' - 0 3/4" | 0' - 0 7/16" | 0' - 0 5/16" |
| W14X30 | 8.85 in² | 30 | 0' - 6 3/4" | 1' - 1 13/16" | 0' - 1 1/8" | 0' - 0 3/4" | 0' - 0 3/8" | 0' - 0 1/4" |
| W14X26 | 7.69 in² | 26 | 0' - 5" | 1' - 1 7/8" | 0' - 1 1/8" | 0' - 0 11/16" | 0' - 0 7/16" | 0' - 0 1/4" |
| W14X22 | 6.49 in² | 22 | 0' - 5" | 1' - 1 11/16" | 0' - 1 1/16" | 0' - 0 3/4" | 0' - 0 5/16" | 0' - 0 1/4" |
| W12X336 | 98.8 in² | 336 | 1' - 1 3/8" | 1' - 4 13/16" | 0' - 3 7/8" | 0' - 0 15/16" | 0' - 2 15/16" | 0' - 1 3/4" |
| W12X305 | 89.6 in² | 305 | 1' - 1 3/16" | 1' - 4 5/16" | 0' - 3 5/8" | 0' - 0 15/16" | 0' - 2 11/16" | 0' - 1 5/8" |
| W12X279 | 81.9 in² | 279 | 1' - 1 1/8" | 1' - 3 7/8" | 0' - 3 3/8" | 0' - 0 7/8" | 0' - 2 1/2" | 0' - 1 1/2" |
| W12X252 | 74 in² | 252 | 1' - 1" | 1' - 3 3/8" | 0' - 3 1/8" | 0' - 0 7/8" | 0' - 2 1/4" | 0' - 1 3/8" |
| W12X230 | 67.7 in² | 230 | 1' - 0 7/8" | 1' - 3 1/8" | 0' - 2 15/16" | 0' - 0 7/8" | 0' - 2 1/16" | 0' - 1 5/16" |
| W12X210 | 61.8 in² | 210 | 1' - 0 13/16" | 1' - 2 11/16" | 0' - 2 13/16" | 0' - 0 15/16" | 0' - 1 7/8" | 0' - 1 3/16" |
| W12X190 | 55.8 in² | 190 | 1' - 0 11/16" | 1' - 2 3/8" | 0' - 2 5/8" | 0' - 0 7/8" | 0' - 1 3/4" | 0' - 1 1/16" |
| W12X170 | 50 in² | 170 | 1' - 0 5/8" | 1' - 2" | 0' - 2 7/16" | 0' - 0 7/8" | 0' - 1 9/16" | 0' - 0 15/16" |
| W12X152 | 44.7 in² | 152 | 1' - 0 1/2" | 1' - 1 11/16" | 0' - 2 5/16" | 0' - 0 15/16" | 0' - 1 3/8" | 0' - 0 7/8" |
| W12X136 | 39.9 in² | 136 | 1' - 0 3/8" | 1' - 1 3/8" | 0' - 2 1/8" | 0' - 0 7/8" | 0' - 1 1/4" | 0' - 0 13/16" |
| W12X120 | 35.3 in² | 120 | 1' - 0 5/16" | 1' - 1 1/8" | 0' - 2" | 0' - 0 7/8" | 0' - 1 1/8" | 0' - 0 11/16" |
| W12X106 | 31.2 in² | 106 | 1' - 0 3/16" | 1' - 0 7/8" | 0' - 1 7/8" | 0' - 0 7/8" | 0' - 1" | 0' - 0 5/8" |
| W12X96 | 28.2 in² | 96 | 1' - 0 3/16" | 1' - 0 11/16" | 0' - 1 13/16" | 0' - 0 15/16" | 0' - 0 7/8" | 0' - 0 9/16" |
| W12X87 | 25.6 in² | 87 | 1' - 0 1/8" | 1' - 0 1/2" | 0' - 1 11/16" | 0' - 0 7/8" | 0' - 0 13/16" | 0' - 0 1/2" |
| W12X79 | 23.2 in² | 79 | 1' - 0 1/8" | 1' - 0 3/8" | 0' - 1 5/8" | 0' - 0 7/8" | 0' - 0 3/4" | 0' - 0 1/2" |
| W12X72 | 21.1 in² | 72 | 1' - 0" | 1' - 0 5/16" | 0' - 1 9/16" | 0' - 0 7/8" | 0' - 0 11/16" | 0' - 0 7/16" |
| W12X65 | 19.1 in² | 65 | 1' - 0" | 1' - 0 1/8" | 0' - 1 1/2" | 0' - 0 7/8" | 0' - 0 5/8" | 0' - 0 3/8" |
| W12X58 | 17 in² | 58 | 0' - 10" | 1' - 0 3/16" | 0' - 1 1/2" | 0' - 0 7/8" | 0' - 0 5/8" | 0' - 0 3/8" |
| W12X53 | 15.6 in² | 53 | 0' - 10" | 1' - 0 1/8" | 0' - 1 3/8" | 0' - 0 13/16" | 0' - 0 9/16" | 0' - 0 3/8" |
| W12X50 | 14.6 in² | 50 | 0' - 8 1/16" | 1' - 0 3/16" | 0' - 1 1/2" | 0' - 0 7/8" | 0' - 0 5/8" | 0' - 0 3/8" |
| W12X45 | 13.1 in² | 45 | 0' - 8 1/16" | 1' - 0 1/8" | 0' - 1 3/8" | 0' - 0 13/16" | 0' - 0 9/16" | 0' - 0 5/16" |
| W12X40 | 11.7 in² | 40 | 0' - 8" | 0' - 11 7/8" | 0' - 1 3/8" | 0' - 0 7/8" | 0' - 0 1/2" | 0' - 0 5/16" |
| W12X35 | 10.3 in² | 35 | 0' - 6 9/16" | 1' - 0 1/2" | 0' - 1 3/16" | 0' - 0 11/16" | 0' - 0 1/2" | 0' - 0 5/16" |
| W12X30 | 8.79 in² | 30 | 0' - 6 1/2" | 1' - 0 5/16" | 0' - 1 1/8" | 0' - 0 11/16" | 0' - 0 7/16" | 0' - 0 1/4" |
| W12X26 | 7.65 in² | 26 | 0' - 6 1/2" | 1' - 0 3/16" | 0' - 1 1/16" | 0' - 0 11/16" | 0' - 0 3/8" | 0' - 0 1/4" |
| W12X22 | 6.48 in² | 22 | 0' - 4" | 1' - 0 5/16" | 0' - 0 15/16" | 0' - 0 1/2" | 0' - 0 7/16" | 0' - 0 1/4" |
| W12X19 | 5.57 in² | 19 | 0' - 4" | 1' - 0 3/16" | 0' - 0 7/8" | 0' - 0 1/2" | 0' - 0 3/8" | 0' - 0 1/4" |
| W12X16 | 4.71 in² | 16 | 0' - 4" | 1' - 0" | 0' - 0 13/16" | 0' - 0 9/16" | 0' - 0 1/4" | 0' - 0 1/4" |
| W12X14 | 4.16 in² | 14 | 0' - 4" | 0' - 11 7/8" | 0' - 0 3/4" | 0' - 0 1/2" | 0' - 0 1/4" | 0' - 0 3/16" |
| W10X112 | 32.9 in² | 112 | 0' - 10 3/8" | 0' - 11 3/8" | 0' - 1 15/16" | 0' - 0 11/16" | 0' - 1 1/4" | 0' - 0 3/4" |
| W10X100 | 29.4 in² | 100 | 0' - 10 5/16" | 0' - 11 1/8" | 0' - 1 13/16" | 0' - 0 11/16" | 0' - 1 1/8" | 0' - 0 11/16" |
| W10X88 | 25.9 in² | 88 | 0' - 10 5/16" | 0' - 10 13/16" | 0' - 1 11/16" | 0' - 0 11/16" | 0' - 1" | 0' - 0 5/8" |
| W10X77 | 22.6 in² | 77 | 0' - 10 3/16" | 0' - 10 5/8" | 0' - 1 9/16" | 0' - 0 11/16" | 0' - 0 7/8" | 0' - 0 1/2" |
| W10X68 | 20 in² | 68 | 0' - 10 1/8" | 0' - 10 3/8" | 0' - 1 7/16" | 0' - 0 11/16" | 0' - 0 3/4" | 0' - 0 1/2" |
| W10X60 | 17.6 in² | 60 | 0' - 10 1/8" | 0' - 10 3/16" | 0' - 1 3/8" | 0' - 0 11/16" | 0' - 0 11/16" | 0' - 0 7/16" |
| W10X54 | 15.8 in² | 54 | 0' - 10" | 0' - 10 1/8" | 0' - 1 5/16" | 0' - 0 11/16" | 0' - 0 5/8" | 0' - 0 3/8" |
| W10X49 | 14.4 in² | 49 | 0' - 10" | 0' - 10" | 0' - 1 1/4" | 0' - 0 11/16" | 0' - 0 9/16" | 0' - 0 5/16" |
| W10X45 | 13.3 in² | 45 | 0' - 8" | 0' - 10 1/8" | 0' - 1 5/16" | 0' - 0 11/16" | 0' - 0 5/8" | 0' - 0 3/8" |
| W10X39 | 11.5 in² | 39 | 0' - 8" | 0' - 9 15/16" | 0' - 1 3/16" | 0' - 0 11/16" | 0' - 0 1/2" | 0' - 0 5/16" |
| W10X33 | 9.71 in² | 33 | 0' - 7 15/16" | 0' - 9 3/4" | 0' - 1 1/8" | 0' - 0 11/16" | 0' - 0 7/16" | 0' - 0 5/16" |
| W10X30 | 8.84 in² | 30 | 0' - 5 13/16" | 0' - 10 1/2" | 0' - 1 1/8" | 0' - 0 5/8" | 0' - 0 1/2" | 0' - 0 5/16" |
| W10X26 | 7.61 in² | 26 | 0' - 5 3/4" | 0' - 10 5/16" | 0' - 1 1/16" | 0' - 0 5/8" | 0' - 0 7/16" | 0' - 0 1/4" |
| W10X22 | 6.49 in² | 22 | 0' - 5 3/4" | 0' - 10 3/16" | 0' - 0 15/16" | 0' - 0 9/16" | 0' - 0 3/8" | 0' - 0 1/4" |
| W10X19 | 5.62 in² | 19 | 0' - 4" | 0' - 10 3/16" | 0' - 0 15/16" | 0' - 0 9/16" | 0' - 0 3/8" | 0' - 0 1/4" |
| W10X17 | 4.99 in² | 17 | 0' - 4" | 0' - 10 1/8" | 0' - 0 7/8" | 0' - 0 9/16" | 0' - 0 5/16" | 0' - 0 1/4" |
| W10X15 | 4.41 in² | 15 | 0' - 4" | 0' - 10" | 0' - 0 13/16" | 0' - 0 9/16" | 0' - 0 1/4" | 0' - 0 1/4" |
| W10X12 | 3.54 in² | 12 | 0' - 3 15/16" | 0' - 9 7/8" | 0' - 0 3/4" | 0' - 0 9/16" | 0' - 0 3/16" | 0' - 0 3/16" |
| W8X67 | 19.7 in² | 67 | 0' - 8 1/4" | 0' - 9" | 0' - 1 5/8" | 0' - 0 11/16" | 0' - 0 15/16" | 0' - 0 9/16" |
| W8X58 | 17.1 in² | 58 | 0' - 8 1/4" | 0' - 8 3/4" | 0' - 1 1/2" | 0' - 0 11/16" | 0' - 0 13/16" | 0' - 0 1/2" |
| W8X48 | 14.1 in² | 48 | 0' - 8 1/8" | 0' - 8 1/2" | 0' - 1 3/8" | 0' - 0 11/16" | 0' - 0 11/16" | 0' - 0 3/8" |
| W8X40 | 11.7 in² | 40 | 0' - 8 1/16" | 0' - 8 1/4" | 0' - 1 1/4" | 0' - 0 11/16" | 0' - 0 9/16" | 0' - 0 3/8" |
| W8X35 | 10.3 in² | 35 | 0' - 8" | 0' - 8 1/8" | 0' - 1 3/16" | 0' - 0 11/16" | 0' - 0 1/2" | 0' - 0 5/16" |
| W8X31 | 9.12 in² | 31 | 0' - 8" | 0' - 8" | 0' - 1 1/8" | 0' - 0 11/16" | 0' - 0 7/16" | 0' - 0 5/16" |
| W8X28 | 8.24 in² | 28 | 0' - 6 9/16" | 0' - 8 1/16" | 0' - 0 15/16" | 0' - 0 1/2" | 0' - 0 7/16" | 0' - 0 5/16" |
| W8X24 | 7.08 in² | 24 | 0' - 6 1/2" | 0' - 7 15/16" | 0' - 0 7/8" | 0' - 0 1/2" | 0' - 0 3/8" | 0' - 0 1/4" |
| W8X21 | 6.16 in² | 21 | 0' - 5 1/4" | 0' - 8 1/4" | 0' - 0 7/8" | 0' - 0 1/2" | 0' - 0 3/8" | 0' - 0 1/4" |
| W8X18 | 5.26 in² | 18 | 0' - 5 1/4" | 0' - 8 1/8" | 0' - 0 13/16" | 0' - 0 1/2" | 0' - 0 5/16" | 0' - 0 1/4" |
| W8X15 | 4.44 in² | 15 | 0' - 4" | 0' - 8 1/8" | 0' - 0 13/16" | 0' - 0 1/2" | 0' - 0 5/16" | 0' - 0 1/4" |
| W8X13 | 3.84 in² | 13 | 0' - 4" | 0' - 8" | 0' - 0 3/4" | 0' - 0 1/2" | 0' - 0 1/4" | 0' - 0 1/4" |
| W8X10 | 2.96 in² | 10 | 0' - 3 15/16" | 0' - 7 7/8" | 0' - 0 11/16" | 0' - 0 1/2" | 0' - 0 3/16" | 0' - 0 3/16" |
| W6X25 | 7.34 in² | 25 | 0' - 6 1/16" | 0' - 6 3/8" | 0' - 0 15/16" | 0' - 0 1/2" | 0' - 0 7/16" | 0' - 0 5/16" |
| W6X20 | 5.87 in² | 20 | 0' - 6" | 0' - 6 3/16" | 0' - 0 7/8" | 0' - 0 1/2" | 0' - 0 3/8" | 0' - 0 1/4" |
| W6X15 | 4.43 in² | 15 | 0' - 6" | 0' - 6" | 0' - 0 3/4" | 0' - 0 1/2" | 0' - 0 1/4" | 0' - 0 1/4" |
| W6X16 | 4.74 in² | 16 | 0' - 4" | 0' - 6 1/4" | 0' - 0 7/8" | 0' - 0 1/2" | 0' - 0 3/8" | 0' - 0 1/4" |
| W6X12 | 3.55 in² | 12 | 0' - 4" | 0' - 6" | 0' - 0 3/4" | 0' - 0 1/2" | 0' - 0 1/4" | 0' - 0 1/4" |
| W6X9 | 2.68 in² | 9 | 0' - 3 15/16" | 0' - 5 7/8" | 0' - 0 11/16" | 0' - 0 1/2" | 0' - 0 3/16" | 0' - 0 3/16" |
| W6X8.5 | 2.52 in² | 8.5 | 0' - 3 15/16" | 0' - 5 13/16" | 0' - 0 11/16" | 0' - 0 1/2" | 0' - 0 3/16" | 0' - 0 3/16" |
| W5X19 | 5.56 in² | 19 | 0' - 5" | 0' - 5 1/8" | 0' - 0 13/16" | 0' - 0 3/8" | 0' - 0 7/16" | 0' - 0 1/4" |
| W5X16 | 4.71 in² | 16 | 0' - 5" | 0' - 5" | 0' - 0 3/4" | 0' - 0 3/8" | 0' - 0 3/8" | 0' - 0 1/4" |
| W4X13 | 3.83 in² | 13 | 0' - 4 1/16" | 0' - 4 3/16" | 0' - 0 3/4" | 0' - 0 3/8" | 0' - 0 3/8" | 0' - 0 1/4" |

## geometry (parser evidence)
native form markers: Sweep x1
no freeform markers — native parametric forms only
